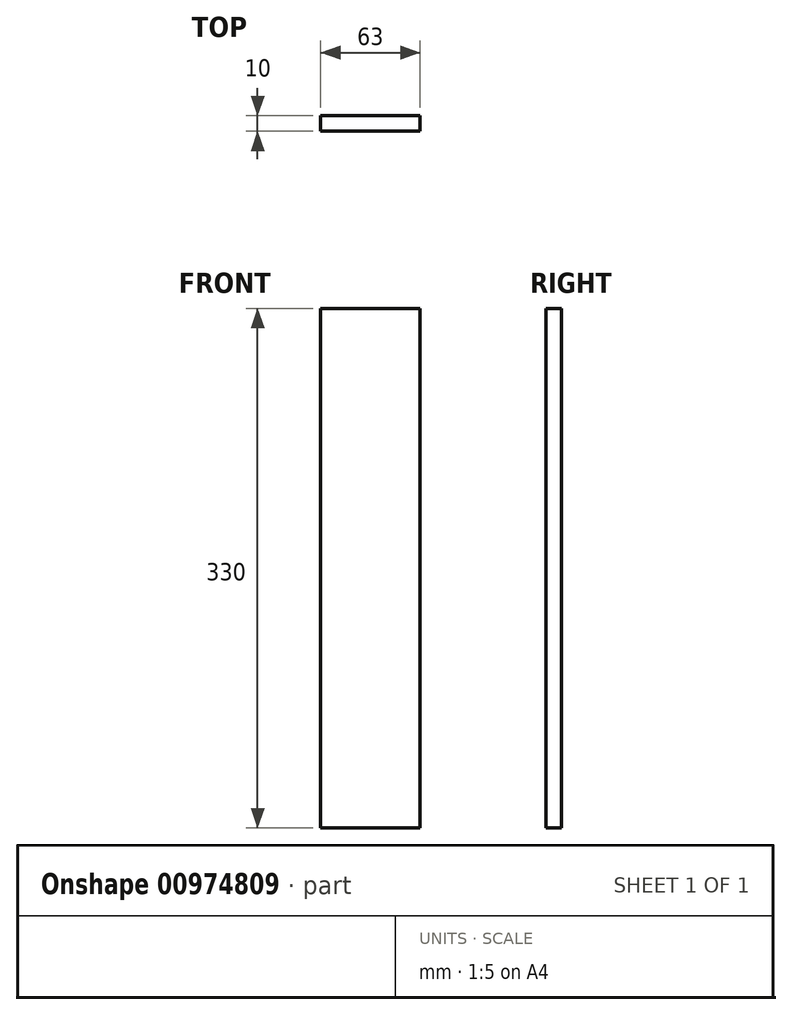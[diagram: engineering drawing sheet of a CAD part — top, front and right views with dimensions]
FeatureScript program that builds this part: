
annotation { "Feature Type Name" : "Feature", "Feature Type Description" : "" }
export const myFeature = defineFeature(function(context is Context, id is Id, definition is map)
    precondition{}
    {
        {
            var Q0;
            Q0=qCreatedBy(makeId("Front.planeOp"),FACE);
            var sketch = newSketch(context, id + "F0", { "sketchPlane" : qUnion([Q0])});
            skLineSegment(sketch, "E0.bottom", {"start": v(31.5, -165) * mm, "end": v(-31.5, -165) * mm});
            skLineSegment(sketch, "E0.top", {"start": v(31.5, 165) * mm, "end": v(-31.5, 165) * mm});
            skLineSegment(sketch, "E0.left", {"start": v(31.5, -165) * mm, "end": v(31.5, 165) * mm});
            skLineSegment(sketch, "E0.right", {"start": v(-31.5, -165) * mm, "end": v(-31.5, 165) * mm});
            skPoint(sketch, "E0.middle", {"position": v(0, 0) * mm});
            skSolve(sketch);
        }
        {
            var Q0;
            Q0 = qSketchRegion(id + "F0", true);
            extrude(context, id + "F1", {"entities" : qUnion([Q0]), "endBound" : BoundingType.SYMMETRIC, "depth" : 10 * mm, "offsetDistance" : 25 * mm});
        }
    });
